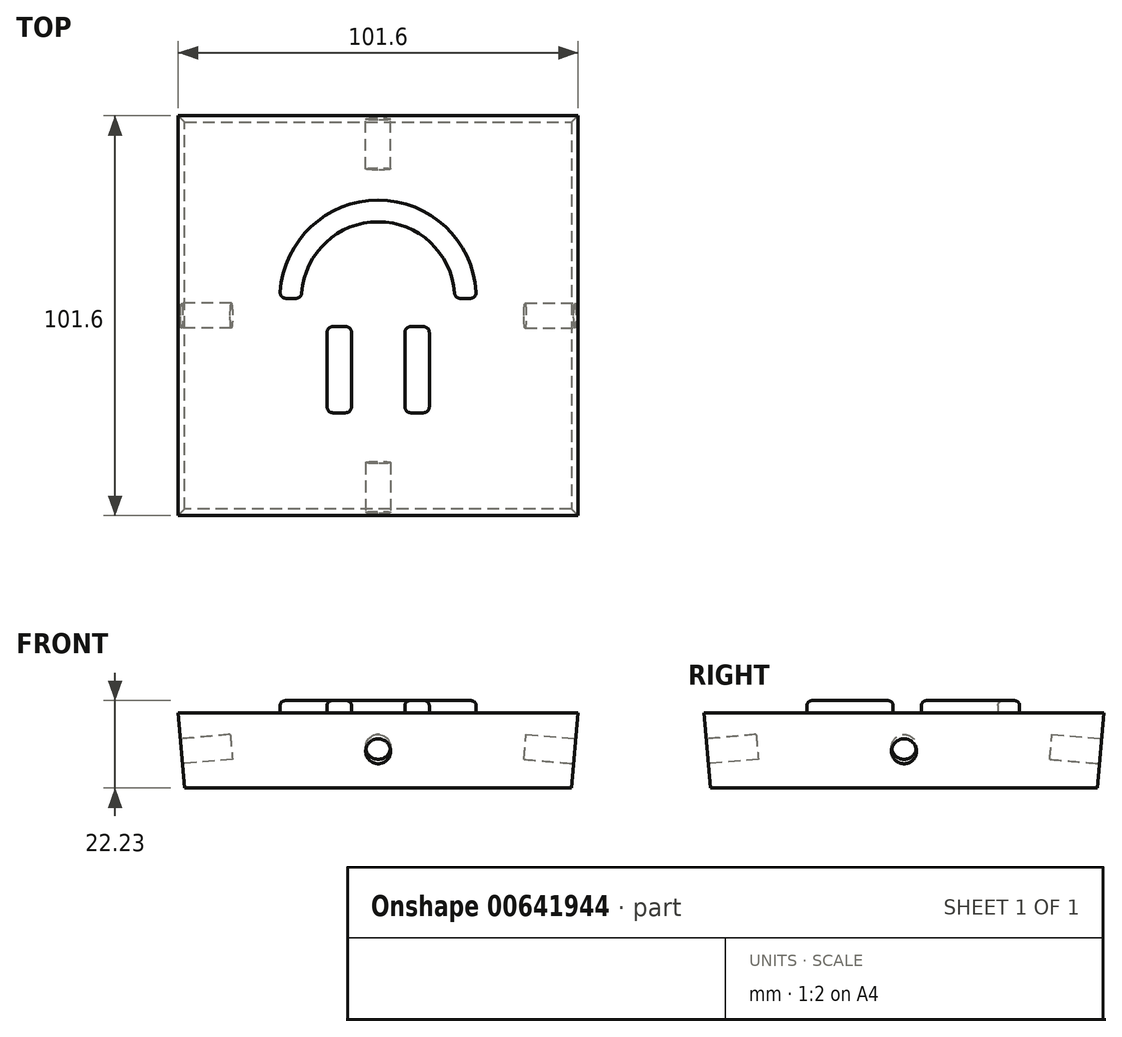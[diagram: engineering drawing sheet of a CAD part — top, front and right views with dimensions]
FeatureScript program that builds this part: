
annotation { "Feature Type Name" : "Feature", "Feature Type Description" : "" }
export const myFeature = defineFeature(function(context is Context, id is Id, definition is map)
    precondition{}
    {
        {
            var Q0;
            Q0=qCreatedBy(makeId("Top.planeOp"),FACE);
            var sketch = newSketch(context, id + "F0", { "sketchPlane" : qUnion([Q0])});
            skLineSegment(sketch, "E0.bottom", {"start": v(-50.8, 50.8) * mm, "end": v(50.8, 50.8) * mm});
            skLineSegment(sketch, "E0.top", {"start": v(-50.8, -50.8) * mm, "end": v(50.8, -50.8) * mm});
            skLineSegment(sketch, "E0.left", {"start": v(-50.8, 50.8) * mm, "end": v(-50.8, -50.8) * mm});
            skLineSegment(sketch, "E0.right", {"start": v(50.8, 50.8) * mm, "end": v(50.8, -50.8) * mm});
            skPoint(sketch, "E0.middle", {"position": v(0, 0) * mm});
            skSolve(sketch);
        }
        {
            var Q0;
            Q0=makeQuery(id+"F0.imprint","IMPRINT",FACE,{"disambiguationData":[TD([[makeQuery(id+"F0.imprint","IMPRINT",EDGE,{"derivedFrom":sQuery(id+"F0.wireOp",EDGE,"E0.bottom")}),-1.0]])]});
            extrude(context, id + "F1", {"entities" : qUnion([Q0]), "depth" : 19.05 * mm, "offsetDistance" : 25.4 * mm});
        }
        {
            var Q0;
            Q0=makeQuery(id+"F1.opExtrude","CAP_EDGE",EDGE,{"disambiguationData":[OSD([sQuery(id+"F0.wireOp",EDGE,"E0.right")])],"isStart":false});
            var Q1;
            Q1=makeQuery(id+"F1.opExtrude","CAP_EDGE",EDGE,{"disambiguationData":[OSD([sQuery(id+"F0.wireOp",EDGE,"E0.top")])],"isStart":false});
            var Q2;
            Q2=makeQuery(id+"F1.opExtrude","CAP_EDGE",EDGE,{"disambiguationData":[OSD([sQuery(id+"F0.wireOp",EDGE,"E0.left")])],"isStart":false});
            var Q3;
            Q3=makeQuery(id+"F1.opExtrude","CAP_EDGE",EDGE,{"disambiguationData":[OSD([sQuery(id+"F0.wireOp",EDGE,"E0.bottom")])],"isStart":false});
            chamfer(context, id + "F2", {"entities" : qUnion([Q0, Q1, Q2, Q3]), "chamferType" : ChamferType.OFFSET_ANGLE, "width" : 19.05 * mm, "oppositeDirection" : false, "angle" : 5 * degree, "tangentPropagation" : true});
        }
        {
            var Q0;
            Q0=makeQuery(id+"F2.opChamfer","BLEND_FACE",FACE,{"disambiguationData":[OSD([sQuery(id+"F0.wireOp",EDGE,"E0.bottom")])]});
            var sketch = newSketch(context, id + "F3", { "sketchPlane" : qUnion([Q0])});
            skLineSegment(sketch, "E1", {"start": v(-49.13, 14.7) * mm, "end": v(50.8, -4.43) * mm, "construction": true});
            skLineSegment(sketch, "E2", {"start": v(-50.8, -4.43) * mm, "end": v(49.13, 14.7) * mm, "construction": true});
            skCircle(sketch, "E3", {"center": v(0, 5.3) * mm, "radius": 3.18 * mm});
            skSolve(sketch);
        }
        {
            var Q0;
            Q0=makeQuery(id+"F3.imprint","IMPRINT",FACE,{"disambiguationData":[TD([[makeQuery(id+"F3.imprint","IMPRINT",EDGE,{"derivedFrom":sQuery(id+"F3.wireOp",EDGE,"E3")}),1.0]])]});
            extrude(context, id + "F4", {"entities" : qUnion([Q0]), "operationType" : NewBodyOperationType.REMOVE, "oppositeDirection" : true, "depth" : 12.7 * mm, "offsetDistance" : 25.4 * mm});
        }
        {
            var Q0;
            Q0=makeQuery(id+"F2.opChamfer","BLEND_FACE",FACE,{"disambiguationData":[OSD([sQuery(id+"F0.wireOp",EDGE,"E0.left")])]});
            var sketch = newSketch(context, id + "F5", { "sketchPlane" : qUnion([Q0])});
            skLineSegment(sketch, "E4", {"start": v(-49.13, 14.7) * mm, "end": v(50.8, -4.43) * mm, "construction": true});
            skLineSegment(sketch, "E5", {"start": v(-50.8, -4.43) * mm, "end": v(49.13, 14.7) * mm, "construction": true});
            skCircle(sketch, "E6", {"center": v(0, 5.3) * mm, "radius": 3.18 * mm});
            skSolve(sketch);
        }
        {
            var Q0;
            Q0=makeQuery(id+"F2.opChamfer","BLEND_FACE",FACE,{"disambiguationData":[OSD([sQuery(id+"F0.wireOp",EDGE,"E0.top")])]});
            var sketch = newSketch(context, id + "F6", { "sketchPlane" : qUnion([Q0])});
            skLineSegment(sketch, "E7", {"start": v(-49.13, 14.7) * mm, "end": v(50.8, -4.43) * mm, "construction": true});
            skLineSegment(sketch, "E8", {"start": v(-50.8, -4.43) * mm, "end": v(49.13, 14.7) * mm, "construction": true});
            skCircle(sketch, "E9", {"center": v(0, 5.3) * mm, "radius": 3.18 * mm});
            skSolve(sketch);
        }
        {
            var Q0;
            Q0=makeQuery(id+"F2.opChamfer","BLEND_FACE",FACE,{"disambiguationData":[OSD([sQuery(id+"F0.wireOp",EDGE,"E0.right")])]});
            var sketch = newSketch(context, id + "F7", { "sketchPlane" : qUnion([Q0])});
            skLineSegment(sketch, "E10", {"start": v(-49.13, 14.7) * mm, "end": v(50.8, -4.43) * mm, "construction": true});
            skLineSegment(sketch, "E11", {"start": v(-50.8, -4.43) * mm, "end": v(49.13, 14.7) * mm, "construction": true});
            skCircle(sketch, "E12", {"center": v(0, 5.3) * mm, "radius": 3.18 * mm});
            skSolve(sketch);
        }
        {
            var Q0;
            Q0=makeQuery(id+"F7.imprint","IMPRINT",FACE,{"disambiguationData":[TD([[makeQuery(id+"F7.imprint","IMPRINT",EDGE,{"derivedFrom":sQuery(id+"F7.wireOp",EDGE,"E12")}),1.0]])]});
            extrude(context, id + "F8", {"entities" : qUnion([Q0]), "operationType" : NewBodyOperationType.REMOVE, "oppositeDirection" : true, "depth" : 12.7 * mm, "offsetDistance" : 25.4 * mm});
        }
        {
            var Q0;
            Q0=makeQuery(id+"F6.imprint","IMPRINT",FACE,{"disambiguationData":[TD([[makeQuery(id+"F6.imprint","IMPRINT",EDGE,{"derivedFrom":sQuery(id+"F6.wireOp",EDGE,"E9")}),1.0]])]});
            extrude(context, id + "F9", {"entities" : qUnion([Q0]), "operationType" : NewBodyOperationType.REMOVE, "oppositeDirection" : true, "depth" : 12.7 * mm, "offsetDistance" : 25.4 * mm});
        }
        {
            var Q0;
            Q0=makeQuery(id+"F5.imprint","IMPRINT",FACE,{"disambiguationData":[TD([[makeQuery(id+"F5.imprint","IMPRINT",EDGE,{"derivedFrom":sQuery(id+"F5.wireOp",EDGE,"E6")}),1.0]])]});
            extrude(context, id + "F10", {"entities" : qUnion([Q0]), "operationType" : NewBodyOperationType.REMOVE, "oppositeDirection" : true, "depth" : 12.7 * mm, "offsetDistance" : 25.4 * mm});
        }
        {
            var Q0;
            Q0=makeQuery(id+"F1.opExtrude","CAP_FACE",FACE,{"disambiguationData":[OSD([sQuery(id+"F0.wireOp",EDGE,"E0.bottom"),sQuery(id+"F0.wireOp",EDGE,"E0.top"),sQuery(id+"F0.wireOp",EDGE,"E0.left"),sQuery(id+"F0.wireOp",EDGE,"E0.right")])],"isStart":true});
            var sketch = newSketch(context, id + "F11", { "sketchPlane" : qUnion([Q0])});
            skLineSegment(sketch, "E13.bottom", {"start": v(-11.51, 24.67) * mm, "end": v(-8.25, 24.67) * mm});
            skLineSegment(sketch, "E13.top", {"start": v(-11.51, 2.78) * mm, "end": v(-8.25, 2.78) * mm});
            skLineSegment(sketch, "E13.left", {"start": v(-12.99, 23.2) * mm, "end": v(-12.99, 4.25) * mm});
            skLineSegment(sketch, "E13.right", {"start": v(-6.78, 23.2) * mm, "end": v(-6.78, 4.25) * mm});
            skLineSegment(sketch, "E14", {"start": v(0, 0) * mm, "end": v(0, 24.5) * mm, "construction": true});
            skLineSegment(sketch, "E15.MirrorCS", {"start": v(11.51, 24.67) * mm, "end": v(8.25, 24.67) * mm});
            skLineSegment(sketch, "E16.MirrorCS", {"start": v(11.51, 2.78) * mm, "end": v(8.25, 2.78) * mm});
            skLineSegment(sketch, "E17.MirrorCS", {"start": v(6.78, 23.2) * mm, "end": v(6.78, 4.25) * mm});
            skLineSegment(sketch, "E18.MirrorCS", {"start": v(12.99, 23.2) * mm, "end": v(12.99, 4.25) * mm});
            skArc(sketch, "E19", {"start": v(-19.4, -5.78) * mm, "mid": v(0, -23.86) * mm, "end": v(19.4, -5.78) * mm});
            skArc(sketch, "E20", {"start": v(-24.9, -5.97) * mm, "mid": v(0, -29.36) * mm, "end": v(24.9, -5.97) * mm});
            skLineSegment(sketch, "E21", {"start": v(-23.43, -4.4) * mm, "end": v(-20.87, -4.4) * mm});
            skLineSegment(sketch, "E22.trimOffspring", {"start": v(20.87, -4.4) * mm, "end": v(23.43, -4.4) * mm});
            skPoint(sketch, "E23.visualSharp", {"position": v(-24.95, -4.4) * mm});
            skArc(sketch, "E23.filletArc", {"start": v(-23.43, -4.4) * mm, "mid": v(-24.5, -4.87) * mm, "end": v(-24.9, -5.97) * mm});
            skPoint(sketch, "E24.visualSharp", {"position": v(19.45, -4.4) * mm});
            skArc(sketch, "E24.filletArc", {"start": v(20.87, -4.4) * mm, "mid": v(19.86, -4.8) * mm, "end": v(19.4, -5.78) * mm});
            skPoint(sketch, "E25.visualSharp", {"position": v(-19.45, -4.4) * mm});
            skArc(sketch, "E25.filletArc", {"start": v(-19.4, -5.78) * mm, "mid": v(-19.86, -4.8) * mm, "end": v(-20.87, -4.4) * mm});
            skPoint(sketch, "E26.visualSharp", {"position": v(24.95, -4.4) * mm});
            skArc(sketch, "E26.filletArc", {"start": v(24.9, -5.97) * mm, "mid": v(24.5, -4.87) * mm, "end": v(23.43, -4.4) * mm});
            skPoint(sketch, "E27.visualSharp", {"position": v(6.78, 24.67) * mm});
            skArc(sketch, "E27.filletArc", {"start": v(8.25, 24.67) * mm, "mid": v(7.21, 24.24) * mm, "end": v(6.78, 23.2) * mm});
            skPoint(sketch, "E28.visualSharp", {"position": v(12.99, 24.67) * mm});
            skArc(sketch, "E28.filletArc", {"start": v(12.99, 23.2) * mm, "mid": v(12.56, 24.24) * mm, "end": v(11.51, 24.67) * mm});
            skPoint(sketch, "E29.visualSharp", {"position": v(6.78, 2.78) * mm});
            skArc(sketch, "E29.filletArc", {"start": v(6.78, 4.25) * mm, "mid": v(7.21, 3.2) * mm, "end": v(8.25, 2.78) * mm});
            skPoint(sketch, "E30.visualSharp", {"position": v(12.99, 2.78) * mm});
            skArc(sketch, "E30.filletArc", {"start": v(11.51, 2.78) * mm, "mid": v(12.56, 3.2) * mm, "end": v(12.99, 4.25) * mm});
            skPoint(sketch, "E31.visualSharp", {"position": v(-12.99, 24.67) * mm});
            skArc(sketch, "E31.filletArc", {"start": v(-11.51, 24.67) * mm, "mid": v(-12.56, 24.24) * mm, "end": v(-12.99, 23.2) * mm});
            skPoint(sketch, "E32.visualSharp", {"position": v(-6.78, 24.67) * mm});
            skArc(sketch, "E32.filletArc", {"start": v(-6.78, 23.2) * mm, "mid": v(-7.21, 24.24) * mm, "end": v(-8.25, 24.67) * mm});
            skPoint(sketch, "E33.visualSharp", {"position": v(-12.99, 2.78) * mm});
            skArc(sketch, "E33.filletArc", {"start": v(-12.99, 4.25) * mm, "mid": v(-12.56, 3.2) * mm, "end": v(-11.51, 2.78) * mm});
            skPoint(sketch, "E34.visualSharp", {"position": v(-6.78, 2.78) * mm});
            skArc(sketch, "E34.filletArc", {"start": v(-8.25, 2.78) * mm, "mid": v(-7.21, 3.2) * mm, "end": v(-6.78, 4.25) * mm});
            skSolve(sketch);
        }
        {
            var Q0;
            Q0 = qSketchRegion(id + "F11", true);
            extrude(context, id + "F12", {"entities" : qUnion([Q0]), "operationType" : NewBodyOperationType.ADD, "depth" : 3.17 * mm, "offsetDistance" : 25.4 * mm});
        }
        {
            var Q0;
            Q0=makeQuery(id+"F12.opExtrude","CAP_EDGE",EDGE,{"disambiguationData":[OSD([sQuery(id+"F11.wireOp",EDGE,"E20")])],"isStart":false});
            var Q1;
            Q1=makeQuery(id+"F12.opExtrude","CAP_EDGE",EDGE,{"disambiguationData":[OSD([sQuery(id+"F11.wireOp",EDGE,"E19")])],"isStart":false});
            var Q2;
            Q2=makeQuery(id+"F12.opExtrude","CAP_EDGE",EDGE,{"disambiguationData":[OSD([sQuery(id+"F11.wireOp",EDGE,"E21")])],"isStart":false});
            var Q3;
            Q3=makeQuery(id+"F12.opExtrude","CAP_EDGE",EDGE,{"disambiguationData":[OSD([sQuery(id+"F11.wireOp",EDGE,"E25.filletArc")])],"isStart":false});
            var Q4;
            Q4=makeQuery(id+"F12.opExtrude","CAP_EDGE",EDGE,{"disambiguationData":[OSD([sQuery(id+"F11.wireOp",EDGE,"E23.filletArc")])],"isStart":false});
            var Q5;
            Q5=makeQuery(id+"F12.opExtrude","CAP_EDGE",EDGE,{"disambiguationData":[OSD([sQuery(id+"F11.wireOp",EDGE,"E24.filletArc")])],"isStart":false});
            var Q6;
            Q6=makeQuery(id+"F12.opExtrude","CAP_EDGE",EDGE,{"disambiguationData":[OSD([sQuery(id+"F11.wireOp",EDGE,"E22.trimOffspring")])],"isStart":false});
            var Q7;
            Q7=makeQuery(id+"F12.opExtrude","CAP_EDGE",EDGE,{"disambiguationData":[OSD([sQuery(id+"F11.wireOp",EDGE,"E26.filletArc")])],"isStart":false});
            var Q8;
            Q8=makeQuery(id+"F12.opExtrude","CAP_EDGE",EDGE,{"disambiguationData":[OSD([sQuery(id+"F11.wireOp",EDGE,"E15.MirrorCS")])],"isStart":false});
            var Q9;
            Q9=makeQuery(id+"F12.opExtrude","CAP_EDGE",EDGE,{"disambiguationData":[OSD([sQuery(id+"F11.wireOp",EDGE,"E27.filletArc")])],"isStart":false});
            var Q10;
            Q10=makeQuery(id+"F12.opExtrude","CAP_EDGE",EDGE,{"disambiguationData":[OSD([sQuery(id+"F11.wireOp",EDGE,"E17.MirrorCS")])],"isStart":false});
            var Q11;
            Q11=makeQuery(id+"F12.opExtrude","CAP_EDGE",EDGE,{"disambiguationData":[OSD([sQuery(id+"F11.wireOp",EDGE,"E29.filletArc")])],"isStart":false});
            var Q12;
            Q12=makeQuery(id+"F12.opExtrude","CAP_EDGE",EDGE,{"disambiguationData":[OSD([sQuery(id+"F11.wireOp",EDGE,"E16.MirrorCS")])],"isStart":false});
            var Q13;
            Q13=makeQuery(id+"F12.opExtrude","CAP_EDGE",EDGE,{"disambiguationData":[OSD([sQuery(id+"F11.wireOp",EDGE,"E30.filletArc")])],"isStart":false});
            var Q14;
            Q14=makeQuery(id+"F12.opExtrude","CAP_EDGE",EDGE,{"disambiguationData":[OSD([sQuery(id+"F11.wireOp",EDGE,"E28.filletArc")])],"isStart":false});
            var Q15;
            Q15=makeQuery(id+"F12.opExtrude","CAP_EDGE",EDGE,{"disambiguationData":[OSD([sQuery(id+"F11.wireOp",EDGE,"E18.MirrorCS")])],"isStart":false});
            var Q16;
            Q16=makeQuery(id+"F12.opExtrude","CAP_EDGE",EDGE,{"disambiguationData":[OSD([sQuery(id+"F11.wireOp",EDGE,"E13.right")])],"isStart":false});
            var Q17;
            Q17=makeQuery(id+"F12.opExtrude","CAP_EDGE",EDGE,{"disambiguationData":[OSD([sQuery(id+"F11.wireOp",EDGE,"E32.filletArc")])],"isStart":false});
            var Q18;
            Q18=makeQuery(id+"F12.opExtrude","CAP_EDGE",EDGE,{"disambiguationData":[OSD([sQuery(id+"F11.wireOp",EDGE,"E13.bottom")])],"isStart":false});
            var Q19;
            Q19=makeQuery(id+"F12.opExtrude","CAP_EDGE",EDGE,{"disambiguationData":[OSD([sQuery(id+"F11.wireOp",EDGE,"E31.filletArc")])],"isStart":false});
            var Q20;
            Q20=makeQuery(id+"F12.opExtrude","CAP_EDGE",EDGE,{"disambiguationData":[OSD([sQuery(id+"F11.wireOp",EDGE,"E13.left")])],"isStart":false});
            var Q21;
            Q21=makeQuery(id+"F12.opExtrude","CAP_EDGE",EDGE,{"disambiguationData":[OSD([sQuery(id+"F11.wireOp",EDGE,"E33.filletArc")])],"isStart":false});
            var Q22;
            Q22=makeQuery(id+"F12.opExtrude","CAP_EDGE",EDGE,{"disambiguationData":[OSD([sQuery(id+"F11.wireOp",EDGE,"E13.top")])],"isStart":false});
            var Q23;
            Q23=makeQuery(id+"F12.opExtrude","CAP_EDGE",EDGE,{"disambiguationData":[OSD([sQuery(id+"F11.wireOp",EDGE,"E34.filletArc")])],"isStart":false});
            fillet(context, id + "F13", {"entities" : qUnion([Q0, Q1, Q2, Q3, Q4, Q5, Q6, Q7, Q8, Q9, Q10, Q11, Q12, Q13, Q14, Q15, Q16, Q17, Q18, Q19, Q20, Q21, Q22, Q23]), "radius" : 1.27 * mm, "tangentPropagation" : true, "allowEdgeOverflow" : false});
        }
        {
            var Q0;
            Q0=makeQuery(id+"F1.opExtrude","CAP_FACE",FACE,{"disambiguationData":[OSD([sQuery(id+"F0.wireOp",EDGE,"E0.bottom"),sQuery(id+"F0.wireOp",EDGE,"E0.top"),sQuery(id+"F0.wireOp",EDGE,"E0.left"),sQuery(id+"F0.wireOp",EDGE,"E0.right")])],"isStart":false});
            var sketch = newSketch(context, id + "F14", { "sketchPlane" : qUnion([Q0])});
            skLineSegment(sketch, "E35", {"start": v(55.15, 29.48) * mm, "end": v(55.15, -28.93) * mm, "construction": true});
            skSolve(sketch);
        }
        {
            var Q0;
            Q0=makeQuery(id+"F1.opExtrude","SWEPT_BODY",BODY,{"disambiguationData":[OSD([sQuery(id+"F0.wireOp",EDGE,"E0.bottom"),sQuery(id+"F0.wireOp",EDGE,"E0.top"),sQuery(id+"F0.wireOp",EDGE,"E0.left"),sQuery(id+"F0.wireOp",EDGE,"E0.right")])]});
            var Q1;
            Q1=sQuery(id+"F14.wireOp",EDGE,"E35");
            transform(context, id + "F15", {"entities" : qUnion([Q0]), "transformType" : TransformType.ROTATION, "transformAxis" : qUnion([Q1]), "angle" : 180 * degree, "makeCopy" : false});
        }
    });
